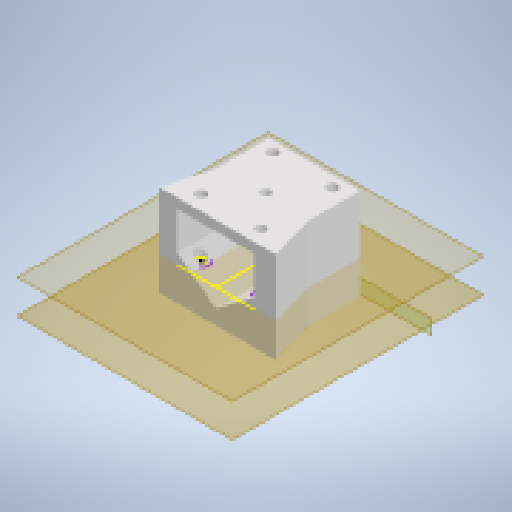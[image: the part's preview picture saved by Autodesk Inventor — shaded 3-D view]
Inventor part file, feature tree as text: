
AUTODESK INVENTOR PART (.ipt)
format: ipt  version: 2024.2 (Build 282272000, 272)  size: 348,672 bytes
history: native  units: mm
features: other x9, sketch x8, extrude x7, projected_geometry x6, reference x5
ambient origin geometry x8: Origin, YZ Plane, XZ Plane, XY Plane, X Axis, Y Axis, Z Axis, Center Point
bodies: Body1 (feature_tree)
feature tree (35):
  other  "Твердое тело1"
  other  "РабПлоскость2"
  extrude  "Выдавливание1"  Depth=1.0mm
  other  "РабПлоскость3"
  extrude  "Выдавливание3"  Depth=1.0mm
  other  "РабПлоскость4"
  extrude  "дырки"  Depth=4.426mm
  sketch  "Эскиз4"
  other  "РабПлоскость5"
  extrude  "Выдавливание5"  Depth=30.0mm TaperAngle=0.0deg
  extrude  "Выдавливание6"  TaperAngle=0.0deg  [1 undecoded]
  extrude  "Выдавливание7"  Depth=9.0mm
  extrude  "Выдавливание9"  Depth=9.0mm
  sketch  "Эскиз1"
  reference  "Ссылка1"
  reference  "Ссылка2"
  reference  "Ссылка3"
  reference  "Ссылка4"
  sketch  "Эскиз2"
  sketch  "Эскиз3"
  projected_geometry  "Спроецированная петля1"
  projected_geometry  "Спроецированная петля2"
  sketch  "Эскиз5"
  projected_geometry  "Спроецированная петля3"
  projected_geometry  "Спроецированная петля4"
  sketch  "Эскиз6"
  projected_geometry  "Спроецированная петля5"
  projected_geometry  "Спроецированная петля6"
  reference  "Ссылка5"
  sketch  "Эскиз7"
  sketch  "Эскиз9"
  other  "<userpath>\Documents\Artist\3D\каретка.iam"
  other  "каретка.iam"
  other  "ANY:5"
  other  "Проецирование ребер1"
note: 1 required parameter value undecoded (feature->parameter linkage not recoverable at this tier; creation-order binding heuristic only, values carry confidence <= 0.55)
